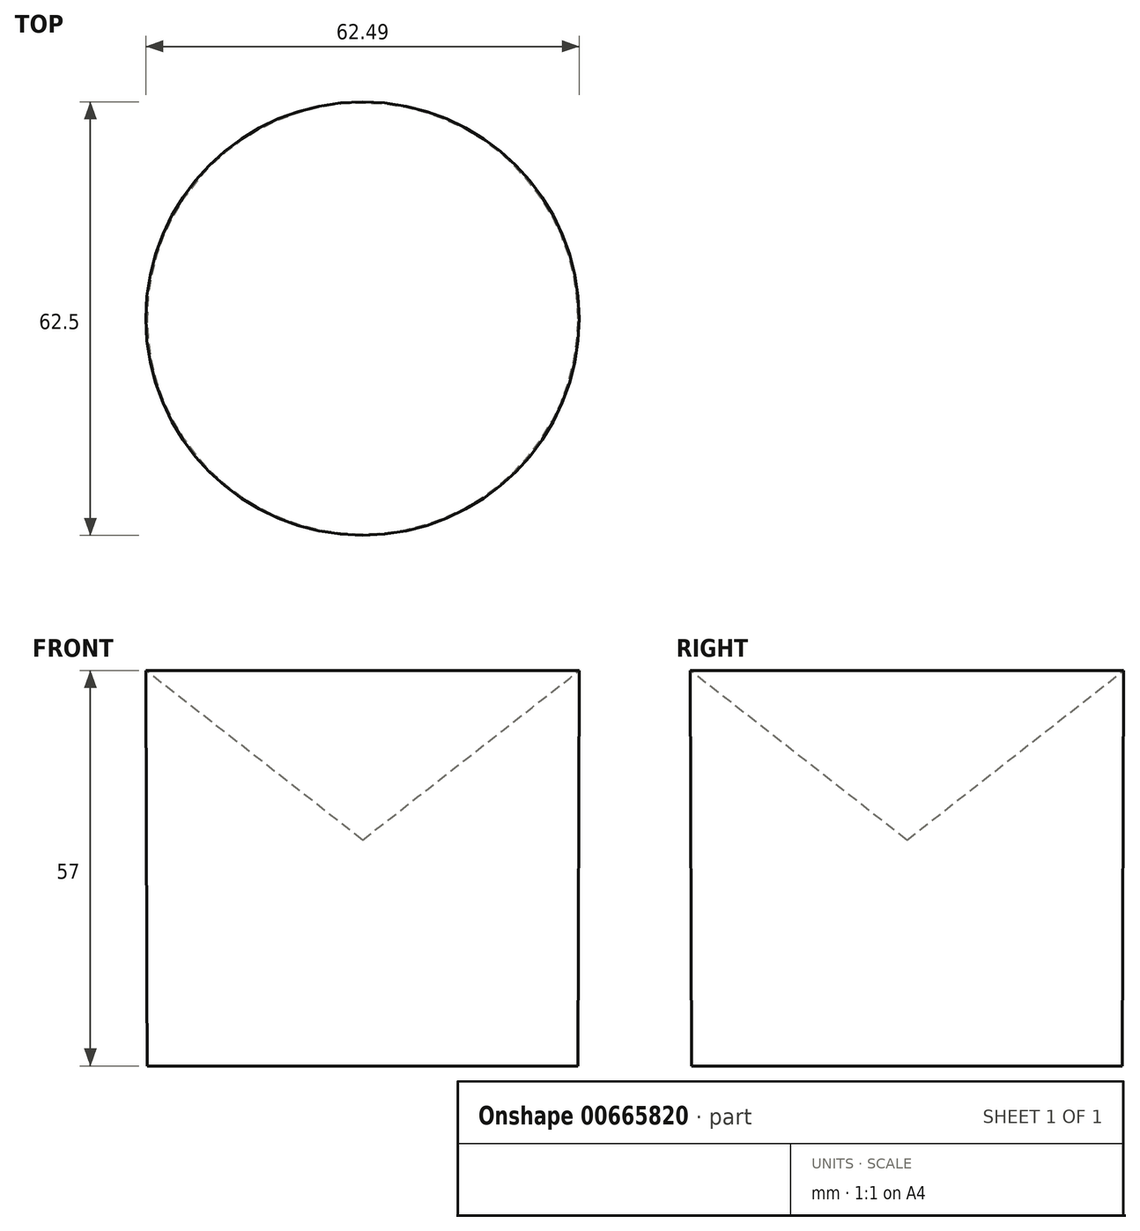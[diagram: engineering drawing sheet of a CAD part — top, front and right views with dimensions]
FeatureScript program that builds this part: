
annotation { "Feature Type Name" : "Feature", "Feature Type Description" : "" }
export const myFeature = defineFeature(function(context is Context, id is Id, definition is map)
    precondition{}
    {
        {
            var Q0;
            Q0=qCreatedBy(makeId("Front.planeOp"),FACE);
            var sketch = newSketch(context, id + "F0", { "sketchPlane" : qUnion([Q0])});
            skLineSegment(sketch, "E0", {"start": v(-44.03, 39.2) * mm, "end": v(-12.78, 14.77) * mm});
            skLineSegment(sketch, "E1", {"start": v(-12.78, 14.77) * mm, "end": v(-12.78, -17.8) * mm});
            skLineSegment(sketch, "E2", {"start": v(-12.78, -17.8) * mm, "end": v(-43.84, -17.8) * mm});
            skLineSegment(sketch, "E3", {"start": v(-43.84, -17.8) * mm, "end": v(-44.03, 39.2) * mm});
            skSolve(sketch);
        }
        {
            var Q0;
            Q0=makeQuery(id+"F0.imprint","IMPRINT",FACE,{"disambiguationData":[TD([[makeQuery(id+"F0.imprint","IMPRINT",EDGE,{"derivedFrom":sQuery(id+"F0.wireOp",EDGE,"E0")}),-1.0]])]});
            var Q1;
            Q1=sQuery(id+"F0.wireOp",EDGE,"E2");
            var Q2;
            Q2=sQuery(id+"F0.wireOp",EDGE,"E3");
            var Q3;
            Q3=sQuery(id+"F0.wireOp",EDGE,"E1");
            revolve(context, id + "F1", {"entities" : qUnion([Q0]), "surfaceEntities" : qUnion([Q1, Q2]), "axis" : qUnion([Q3]), "revolveType" : RevolveType.FULL, "oppositeDirection" : true});
        }
    });
